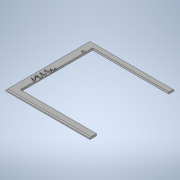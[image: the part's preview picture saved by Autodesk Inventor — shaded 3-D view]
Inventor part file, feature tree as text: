
AUTODESK INVENTOR PART (.ipt)
format: ipt  version: 2021.2 (Build 252289000, 289)  size: 1,715,200 bytes
history: native  units: in
note: dims shown in document units (in); Inventor stores cm internally (conversion verified against a paired STEP export)
features: extrude x1, sketch x1
ambient origin geometry x8: Origin, YZ Plane, XZ Plane, XY Plane, X Axis, Y Axis, Z Axis, Center Point
bodies: Solid1 (feature_tree), Body1 (feature_tree)
feature tree (2):
  extrude  "Extrusion1"  Depth=8.0in TaperAngle=0.0deg
  sketch  "Sketch1"  dims[d0=0.75in d1=0.5in d2=0.0in d3=0.0in d4=8.0in d5=8.0in]
